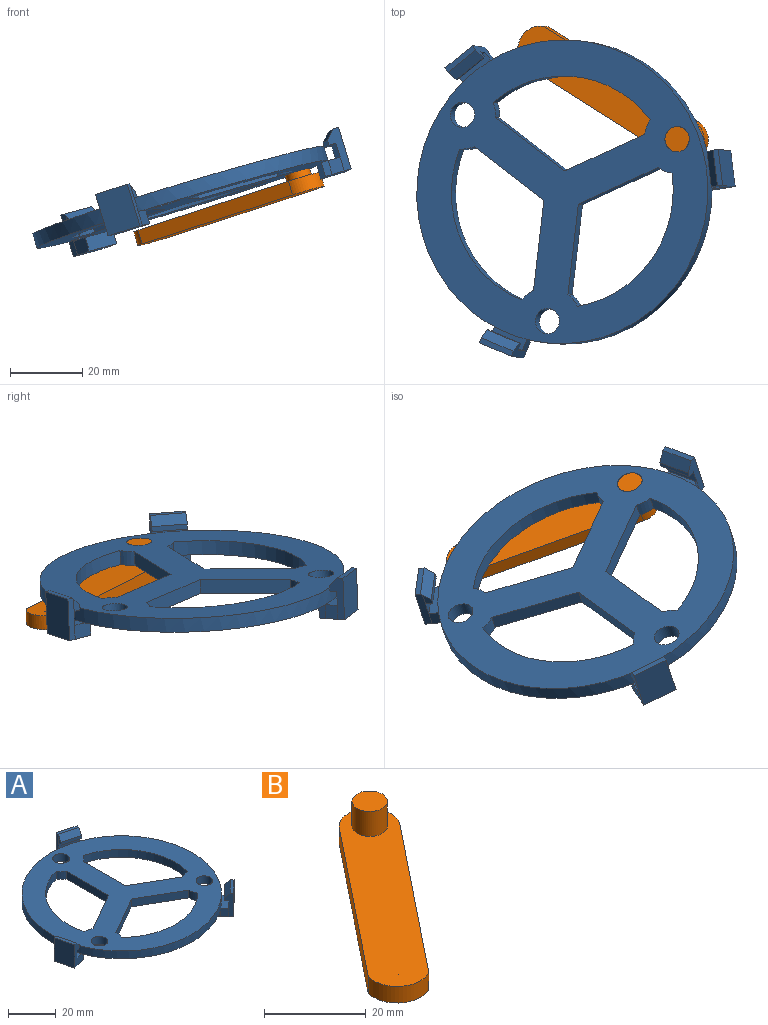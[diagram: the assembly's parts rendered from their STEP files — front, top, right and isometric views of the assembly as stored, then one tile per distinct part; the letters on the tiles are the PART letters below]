
ASSEMBLY  parts=2 mates=1
PART A: 66 faces, bbox 89x88.8x12 mm
  f0: plane 84x84mm, normal (0,0,-1), area 3094.7mm2, adj f1,f2,f3,f4,f5,f6,f7,f8
  f1: plane 25.04x4mm, normal (1,0,0), area 100.1mm2, adj f0,f2,f16,f20
  f2: cylinder r=9.5mm len=4mm, axis (0,0,-1), area 17.4mm2, adj f0,f1,f3,f20
  f3: cylinder r=32mm len=39.47mm, axis (0,0,-1), area 202.9mm2, adj f0,f2,f4,f20
  f4: cylinder r=9.5mm len=4.17mm, axis (0,0,-1), area 17.4mm2, adj f0,f3,f16,f20
  f5: plane 25.04x4mm, normal (-1,0,0), area 100.1mm2, adj f0,f6,f17,f20
  f6: plane 21.68x12.52mm, normal (-0.5,0.87,0), area 100.1mm2, adj f0,f5,f7,f20
  f7: cylinder r=9.5mm len=4.17mm, axis (0,0,-1), area 17.4mm2, adj f0,f6,f8,f20
  f8: cylinder r=32mm len=39.47mm, axis (0,0,-1), area 202.9mm2, adj f0,f7,f17,f20
  f9: plane 21.68x12.52mm, normal (0.5,-0.87,0), area 100.1mm2, adj f0,f10,f18,f20
  f10: plane 21.68x12.52mm, normal (-0.5,-0.87,0), area 100.1mm2, adj f0,f9,f11,f20
  f11: cylinder r=9.5mm len=4.17mm, axis (0,0,-1), area 17.4mm2, adj f0,f10,f12,f20
  f12: cylinder r=32mm len=45.58mm, axis (0,0,-1), area 202.9mm2, adj f0,f11,f18,f20
  f13: cylinder r=3.5mm len=7mm, axis (0,0,-1), area 88mm2, adj f0,f20
  f14: cylinder r=3.5mm len=7mm, axis (0,0,-1), area 88mm2, adj f0,f20
  f15: cylinder r=3.5mm len=7mm, axis (0,0,-1), area 88mm2, adj f0,f20
  f16: plane 21.68x12.52mm, normal (0.5,0.87,0), area 100.1mm2, adj f0,f1,f4,f20
  f17: cylinder r=9.5mm len=4mm, axis (0,0,-1), area 17.4mm2, adj f0,f5,f8,f20
  f18: cylinder r=9.5mm len=4.17mm, axis (0,0,-1), area 17.4mm2, adj f0,f9,f12,f20
  f19: cylinder r=42mm len=84mm, axis (0,0,-1), area 1055.6mm2, adj f0,f20,f29,f36,f51
  f20: plane 84x84mm, normal (0,0,1), area 3160.7mm2, adj f1,f2,f3,f4,f5,f6,f7,f8
  f21: plane 12x3.85mm, normal (0.96,-0.27,0), area 28.9mm2, adj f22,f27,f28,f30,f31,f33,f34,f35
  f22: plane 4x3.39mm, normal (0.97,-0.25,0), area 14mm2, adj f21,f23,f28,f29
  f23: plane 4x1.93mm, normal (0.96,-0.27,0), area 8mm2, adj f0,f22,f24,f28
  f24: plane 9.63x4mm, normal (-0.27,-0.96,0), area 40mm2, adj f0,f23,f25,f28
  f25: plane 5.29x4mm, normal (-0.96,0.27,0), area 22mm2, adj f0,f24,f26,f28,f29
  f26: plane 12x1.94mm, normal (-0.97,0.25,0), area 23.9mm2, adj f25,f27,f28,f30,f31,f32,f35
  f27: plane 12x9.6mm, normal (0.27,0.96,0), area 119.6mm2, adj f21,f26,f28,f31
  f28: plane 11.59x9.94mm, normal (0,0,-1), area 74.8mm2, adj f21,f22,f23,f24,f25,f26,f27
  f29: plane 10.51x6.08mm, normal (0,0,1), area 32.9mm2, adj f19,f22,f25,f30
  f30: plane 9.56x4mm, normal (-0.27,-0.96,0), area 39.7mm2, adj f21,f26,f29,f33
  f31: plane 9.98x4.15mm, normal (0,0,1), area 14.9mm2, adj f21,f26,f27,f35
  f32: plane 3.5x1.93mm, normal (-0.96,0.27,0), area 5mm2, adj f26,f33,f34,f35
  f33: plane 10.1x4.62mm, normal (0,0,-1), area 19.9mm2, adj f21,f30,f32,f34
  f34: plane 9.56x2.69mm, normal (-0.27,-0.96,0), area 14.9mm2, adj f21,f32,f33,f35
  f35: plane 10.24x5.1mm, normal (-0.19,-0.68,0.71), area 35.1mm2, adj f21,f26,f31,f32,f34
  f36: plane 10.55x5.84mm, normal (0,0,1), area 32.9mm2, adj f19,f38,f41,f45
  f37: plane 12x3.88mm, normal (-0.25,0.97,0), area 28.9mm2, adj f38,f43,f44,f45,f46,f48,f49,f50
  f38: plane 4x3.38mm, normal (-0.27,0.96,0), area 14mm2, adj f36,f37,f39,f44
  f39: plane 4x1.94mm, normal (-0.25,0.97,0), area 8mm2, adj f0,f38,f40,f44
  f40: plane 9.69x4mm, normal (0.97,0.25,0), area 40mm2, adj f0,f39,f41,f44
  f41: plane 5.33x4mm, normal (0.25,-0.97,0), area 22mm2, adj f0,f36,f40,f42,f44
  f42: plane 12x1.93mm, normal (0.27,-0.96,0), area 23.9mm2, adj f41,f43,f44,f45,f46,f47,f50
  f43: plane 12x9.66mm, normal (-0.97,-0.25,0), area 119.6mm2, adj f37,f42,f44,f46
  f44: plane 11.58x9.72mm, normal (0,0,-1), area 74.8mm2, adj f37,f38,f39,f40,f41,f42,f43
  f45: plane 9.63x4mm, normal (0.97,0.25,0), area 39.7mm2, adj f36,f37,f42,f48
  f46: plane 10.03x3.9mm, normal (0,0,1), area 14.9mm2, adj f37,f42,f43,f50
  f47: plane 3.5x1.94mm, normal (0.25,-0.97,0), area 5mm2, adj f42,f48,f49,f50
  f48: plane 10.12x4.38mm, normal (0,0,-1), area 19.9mm2, adj f37,f45,f47,f49
  f49: plane 9.63x2.45mm, normal (0.97,0.25,0), area 14.9mm2, adj f37,f47,f48,f50
  f50: plane 10.25x4.87mm, normal (0.69,0.17,0.71), area 35.1mm2, adj f37,f42,f46,f47,f49
  f51: plane 9.6x9.44mm, normal (0,0,1), area 32.9mm2, adj f19,f53,f56,f60
  f52: plane 12x2.86mm, normal (-0.72,-0.7,0), area 28.9mm2, adj f53,f58,f59,f60,f61,f63,f64,f65
  f53: plane 4x2.49mm, normal (-0.7,-0.71,0), area 14mm2, adj f51,f52,f54,f59
  f54: plane 4x1.43mm, normal (-0.72,-0.7,0), area 8mm2, adj f0,f53,f55,f59
  f55: plane 7.16x6.98mm, normal (-0.7,0.72,0), area 40mm2, adj f0,f54,f56,f59
  f56: plane 4x3.94mm, normal (0.72,0.7,0), area 22mm2, adj f0,f51,f55,f57,f59
  f57: plane 12x1.42mm, normal (0.7,0.71,0), area 23.9mm2, adj f56,f58,f59,f60,f61,f62,f65
  f58: plane 12x7.14mm, normal (0.7,-0.72,0), area 119.6mm2, adj f52,f57,f59,f61
  f59: plane 12.42x12.3mm, normal (0,0,-1), area 74.8mm2, adj f52,f53,f54,f55,f56,f57,f58
  f60: plane 7.11x6.93mm, normal (-0.7,0.72,0), area 39.7mm2, adj f51,f52,f57,f63
  f61: plane 8.19x8.01mm, normal (0,0,1), area 14.9mm2, adj f52,f57,f58,f65
  f62: plane 3.5x1.43mm, normal (0.72,0.7,0), area 5mm2, adj f57,f63,f64,f65
  f63: plane 8.51x8.36mm, normal (0,0,-1), area 19.9mm2, adj f52,f60,f62,f64
  f64: plane 7.11x6.93mm, normal (-0.7,0.72,0), area 14.9mm2, adj f52,f62,f63,f65
  f65: plane 8.86x8.72mm, normal (-0.49,0.51,0.71), area 35.1mm2, adj f52,f57,f61,f62,f64
PART B: 11 faces, bbox 42.8x50.4x10 mm
  f0: cylinder r=6mm len=10.69mm, axis (0,0,1), area 75.4mm2, adj f1,f6,f7,f8
  f1: plane 39.86x31.82mm, normal (0.78,-0.62,0), area 204mm2, adj f0,f2,f7,f8
  f2: cylinder r=6.5mm len=9.63mm, axis (0,0,1), area 61.2mm2, adj f1,f6,f7,f8
  f3: cylinder r=32mm len=4mm, axis (0,0,1), area 0.4mm2, adj f4,f5,f7,f8
  f4: plane 4x0.06mm, normal (0.78,-0.62,0), area 0.3mm2, adj f3,f5,f7,f8
  f5: plane 4x0.06mm, normal (0.62,0.78,0), area 0.3mm2, adj f3,f4,f7,f8
  f6: plane 39.86x31.82mm, normal (-0.78,0.62,0), area 204mm2, adj f0,f2,f7,f8
  f7: plane 50.4x42.76mm, normal (0,0,-1), area 703.2mm2, adj f0,f1,f2,f3,f4,f5,f6
  f8: plane 50.4x42.76mm, normal (0,0,1), area 664.7mm2, adj f0,f1,f2,f3,f4,f5,f6,f9
  f9: cylinder r=3.5mm len=7mm, axis (0,0,-1), area 131.9mm2, adj f8,f10
  f10: plane 7x7mm, normal (0,0,1), area 38.5mm2, adj f9
PLACE A rot(axis=(0.11,-0.23,-0.97),68.4deg) t=(-12.91,2.37,-11.1)mm
PLACE B rot(axis=(0.12,-0.18,-0.98),84.2deg) t=(-14.86,12.09,-14.15)mm
MATE revolute B.f9 <-> A.f13  axis (-0.29,0.04,0.96) through (17.64,17.01,1.71)mm
